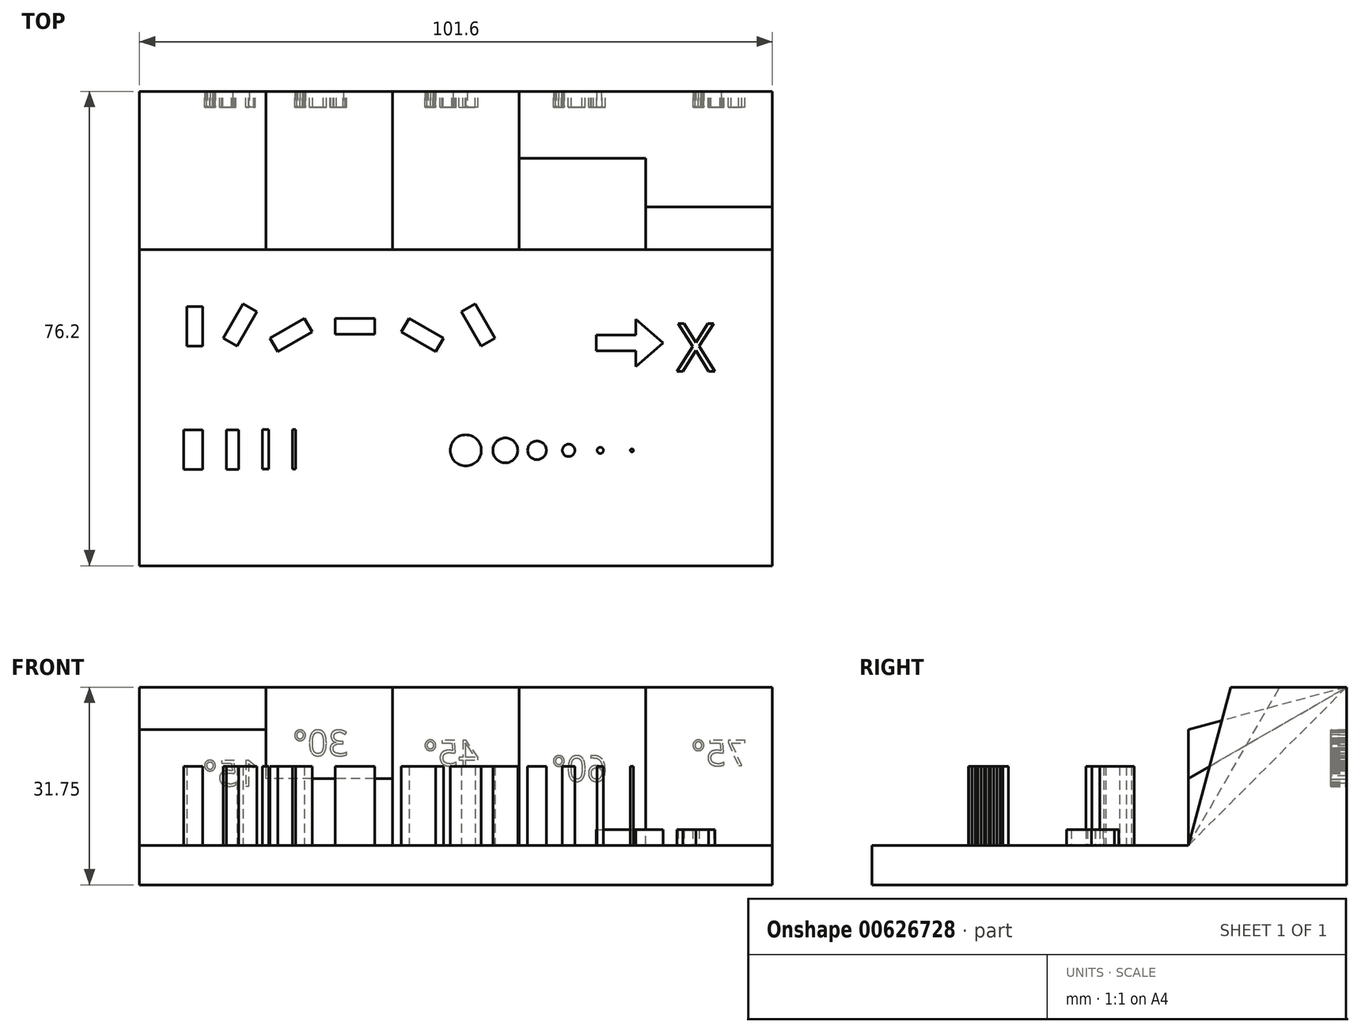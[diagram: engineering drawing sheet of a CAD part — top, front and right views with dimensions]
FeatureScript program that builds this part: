
annotation { "Feature Type Name" : "Feature", "Feature Type Description" : "" }
export const myFeature = defineFeature(function(context is Context, id is Id, definition is map)
    precondition{}
    {
        {
            var Q0;
            Q0=qCreatedBy(makeId("Top.planeOp"),FACE);
            var sketch = newSketch(context, id + "F0", { "sketchPlane" : qUnion([Q0])});
            skLineSegment(sketch, "E0.bottom", {"start": v(-49.6, 47.88) * mm, "end": v(52, 47.88) * mm});
            skLineSegment(sketch, "E0.top", {"start": v(-49.6, -28.32) * mm, "end": v(52, -28.32) * mm});
            skLineSegment(sketch, "E0.left", {"start": v(-49.6, 47.88) * mm, "end": v(-49.6, -28.32) * mm});
            skLineSegment(sketch, "E0.right", {"start": v(52, 47.88) * mm, "end": v(52, -28.32) * mm});
            skSolve(sketch);
        }
        {
            var Q0;
            Q0=makeQuery(id+"F0.imprint","IMPRINT",FACE,{"disambiguationData":[TD([[makeQuery(id+"F0.imprint","IMPRINT",EDGE,{"derivedFrom":sQuery(id+"F0.wireOp",EDGE,"E0.bottom")}),-1.0]])]});
            extrude(context, id + "F1", {"entities" : qUnion([Q0]), "depth" : 6.35 * mm, "offsetDistance" : 25.4 * mm});
        }
        {
            var Q0;
            Q0=makeQuery(id+"F1.opExtrude","CAP_FACE",FACE,{"disambiguationData":[OSD([sQuery(id+"F0.wireOp",EDGE,"E0.bottom"),sQuery(id+"F0.wireOp",EDGE,"E0.top"),sQuery(id+"F0.wireOp",EDGE,"E0.left"),sQuery(id+"F0.wireOp",EDGE,"E0.right")])],"isStart":false});
            var sketch = newSketch(context, id + "F2", { "sketchPlane" : qUnion([Q0])});
            skLineSegment(sketch, "E1.bottom", {"start": v(-49.6, 47.88) * mm, "end": v(52, 47.88) * mm});
            skLineSegment(sketch, "E1.top", {"start": v(-49.6, 22.48) * mm, "end": v(52, 22.48) * mm});
            skLineSegment(sketch, "E1.left", {"start": v(-49.6, 47.88) * mm, "end": v(-49.6, 22.48) * mm});
            skLineSegment(sketch, "E1.right", {"start": v(52, 47.88) * mm, "end": v(52, 22.48) * mm});
            skSolve(sketch);
        }
        {
            var Q0;
            Q0 = qSketchRegion(id + "F2", true);
            extrude(context, id + "F3", {"entities" : qUnion([Q0]), "operationType" : NewBodyOperationType.ADD, "depth" : 25.4 * mm, "offsetDistance" : 25.4 * mm});
        }
        {
            var Q0;
            Q0=makeQuery(id+"F3.boolean.opBoolean","MERGE",FACE,{"derivedFrom":[makeQuery(id+"F1.opExtrude","SWEPT_FACE",FACE,{"disambiguationData":[OSD([sQuery(id+"F0.wireOp",EDGE,"E0.left")])]}),makeQuery(id+"F3.opExtrude","SWEPT_FACE",FACE,{"disambiguationData":[OSD([sQuery(id+"F2.wireOp",EDGE,"E1.left")])]})]});
            var sketch = newSketch(context, id + "F4", { "sketchPlane" : qUnion([Q0])});
            skLineSegment(sketch, "E2", {"start": v(-47.88, 31.75) * mm, "end": v(-22.48, 24.94) * mm});
            skLineSegment(sketch, "E3", {"start": v(-22.48, 24.94) * mm, "end": v(-22.48, 31.75) * mm});
            skLineSegment(sketch, "E4", {"start": v(-22.48, 31.75) * mm, "end": v(-47.88, 31.75) * mm});
            skSolve(sketch);
        }
        {
            var Q0;
            Q0 = qSketchRegion(id + "F4", true);
            extrude(context, id + "F5", {"entities" : qUnion([Q0]), "operationType" : NewBodyOperationType.REMOVE, "oppositeDirection" : true, "depth" : 20.32 * mm, "offsetDistance" : 25.4 * mm});
        }
        {
            var Q0;
            Q0=makeQuery(id+"F5.boolean.opBoolean","COPY",FACE,{"derivedFrom":makeQuery(id+"F5.opExtrude","CAP_FACE",FACE,{"disambiguationData":[OSD([sQuery(id+"F4.wireOp",EDGE,"E2"),sQuery(id+"F4.wireOp",EDGE,"E3"),sQuery(id+"F4.wireOp",EDGE,"E4")])],"isStart":false})});
            var sketch = newSketch(context, id + "F6", { "sketchPlane" : qUnion([Q0])});
            skLineSegment(sketch, "E5", {"start": v(-47.88, 31.75) * mm, "end": v(-22.48, 31.75) * mm});
            skLineSegment(sketch, "E6", {"start": v(-22.48, 31.75) * mm, "end": v(-22.48, 17.09) * mm});
            skLineSegment(sketch, "E7", {"start": v(-22.48, 17.09) * mm, "end": v(-47.88, 31.75) * mm});
            skSolve(sketch);
        }
        {
            var Q0;
            Q0 = qSketchRegion(id + "F6", true);
            extrude(context, id + "F7", {"entities" : qUnion([Q0]), "operationType" : NewBodyOperationType.REMOVE, "oppositeDirection" : true, "depth" : 20.32 * mm, "offsetDistance" : 25.4 * mm});
        }
        {
            var Q0;
            Q0=makeQuery(id+"F7.boolean.opBoolean","COPY",FACE,{"derivedFrom":makeQuery(id+"F7.opExtrude","CAP_FACE",FACE,{"disambiguationData":[OSD([sQuery(id+"F6.wireOp",EDGE,"E5"),sQuery(id+"F6.wireOp",EDGE,"E6"),sQuery(id+"F6.wireOp",EDGE,"E7")])],"isStart":false})});
            var sketch = newSketch(context, id + "F8", { "sketchPlane" : qUnion([Q0])});
            skLineSegment(sketch, "E8", {"start": v(-47.88, 31.75) * mm, "end": v(-22.48, 31.75) * mm});
            skLineSegment(sketch, "E9", {"start": v(-22.48, 31.75) * mm, "end": v(-22.48, 6.35) * mm});
            skLineSegment(sketch, "E10", {"start": v(-22.48, 6.35) * mm, "end": v(-47.88, 31.75) * mm});
            skSolve(sketch);
        }
        {
            var Q0;
            Q0 = qSketchRegion(id + "F8", true);
            extrude(context, id + "F9", {"entities" : qUnion([Q0]), "operationType" : NewBodyOperationType.REMOVE, "oppositeDirection" : true, "depth" : 20.32 * mm, "offsetDistance" : 25.4 * mm});
        }
        {
            var Q0;
            Q0=makeQuery(id+"F9.boolean.opBoolean","COPY",FACE,{"derivedFrom":makeQuery(id+"F9.opExtrude","CAP_FACE",FACE,{"disambiguationData":[OSD([sQuery(id+"F8.wireOp",EDGE,"E8"),sQuery(id+"F8.wireOp",EDGE,"E9"),sQuery(id+"F8.wireOp",EDGE,"E10")])],"isStart":false})});
            var sketch = newSketch(context, id + "F10", { "sketchPlane" : qUnion([Q0])});
            skLineSegment(sketch, "E11", {"start": v(-22.48, 31.75) * mm, "end": v(-22.48, 6.35) * mm});
            skLineSegment(sketch, "E12", {"start": v(-22.48, 6.35) * mm, "end": v(-37.14, 31.75) * mm});
            skLineSegment(sketch, "E13", {"start": v(-37.14, 31.75) * mm, "end": v(-22.48, 31.75) * mm});
            skSolve(sketch);
        }
        {
            var Q0;
            Q0 = qSketchRegion(id + "F10", true);
            extrude(context, id + "F11", {"entities" : qUnion([Q0]), "operationType" : NewBodyOperationType.REMOVE, "oppositeDirection" : true, "depth" : 20.32 * mm, "offsetDistance" : 25.4 * mm});
        }
        {
            var Q0;
            Q0=makeQuery(id+"F11.boolean.opBoolean","COPY",FACE,{"derivedFrom":makeQuery(id+"F11.opExtrude","CAP_FACE",FACE,{"disambiguationData":[OSD([sQuery(id+"F10.wireOp",EDGE,"E11"),sQuery(id+"F10.wireOp",EDGE,"E12"),sQuery(id+"F10.wireOp",EDGE,"E13")])],"isStart":false})});
            var sketch = newSketch(context, id + "F12", { "sketchPlane" : qUnion([Q0])});
            skLineSegment(sketch, "E14", {"start": v(-22.48, 31.75) * mm, "end": v(-22.48, 6.35) * mm});
            skLineSegment(sketch, "E15", {"start": v(-22.48, 6.35) * mm, "end": v(-29.28, 31.75) * mm});
            skLineSegment(sketch, "E16", {"start": v(-29.28, 31.75) * mm, "end": v(-22.48, 31.75) * mm});
            skSolve(sketch);
        }
        {
            var Q0;
            Q0 = qSketchRegion(id + "F12", true);
            extrude(context, id + "F13", {"entities" : qUnion([Q0]), "operationType" : NewBodyOperationType.REMOVE, "oppositeDirection" : true, "depth" : 25.4 * mm, "offsetDistance" : 25.4 * mm});
        }
        {
            var Q0;
            Q0=makeQuery(id+"F3.boolean.opBoolean","MERGE",FACE,{"derivedFrom":[makeQuery(id+"F1.opExtrude","SWEPT_FACE",FACE,{"disambiguationData":[OSD([sQuery(id+"F0.wireOp",EDGE,"E0.bottom")])]}),makeQuery(id+"F3.opExtrude","SWEPT_FACE",FACE,{"disambiguationData":[OSD([sQuery(id+"F2.wireOp",EDGE,"E1.bottom")])]})]});
            var sketch = newSketch(context, id + "F14", { "sketchPlane" : qUnion([Q0])});
            skText(sketch, "E17", { "text": "75°", "fontName": "OpenSans-Regular.ttf"});
            skText(sketch, "E18", { "text": "60°", "fontName": "OpenSans-Regular.ttf"});
            skText(sketch, "E19", { "text": "45°", "fontName": "OpenSans-Regular.ttf"});
            skText(sketch, "E20", { "text": "30°", "fontName": "OpenSans-Regular.ttf"});
            skText(sketch, "E21", { "text": "15°", "fontName": "OpenSans-Regular.ttf"});
            skPoint(sketch, "E22", {"position": v(49.6, 15.87) * mm});
            const initialGuessF14  = {"E17": [-0.0479, 0.01913, 1, 0, 0.00412], "E18": [-0.0255, 0.01662, 1, 0, 0.00412], "E19": [-0.00488, 0.01913, 1, 0, 0.00412], "E20": [0.01604, 0.02074, 1, 0, 0.00412], "E21": [0.0305, 0.01587, 1, 0, 0.00412]};
            skSetInitialGuess(sketch, initialGuessF14);
            skSolve(sketch);
        }
        {
            var Q0;
            Q0=makeQuery(id+"F1.opExtrude","CAP_FACE",FACE,{"disambiguationData":[OSD([sQuery(id+"F0.wireOp",EDGE,"E0.bottom"),sQuery(id+"F0.wireOp",EDGE,"E0.top"),sQuery(id+"F0.wireOp",EDGE,"E0.left"),sQuery(id+"F0.wireOp",EDGE,"E0.right")])],"isStart":false});
            var sketch = newSketch(context, id + "F15", { "sketchPlane" : qUnion([Q0])});
            skLineSegment(sketch, "E23.bottom", {"start": v(-32.96, 13.74) * mm, "end": v(-30.76, 12.47) * mm});
            skLineSegment(sketch, "E23.top", {"start": v(-36.13, 8.24) * mm, "end": v(-33.93, 6.97) * mm});
            skLineSegment(sketch, "E23.left", {"start": v(-32.96, 13.74) * mm, "end": v(-36.13, 8.24) * mm});
            skLineSegment(sketch, "E23.right", {"start": v(-30.76, 12.47) * mm, "end": v(-33.93, 6.97) * mm});
            skLineSegment(sketch, "E24.bottom", {"start": v(-42, 13.32) * mm, "end": v(-39.46, 13.32) * mm});
            skLineSegment(sketch, "E24.top", {"start": v(-42, 6.97) * mm, "end": v(-39.46, 6.97) * mm});
            skLineSegment(sketch, "E24.left", {"start": v(-42, 13.32) * mm, "end": v(-42, 6.97) * mm});
            skLineSegment(sketch, "E24.right", {"start": v(-39.46, 13.32) * mm, "end": v(-39.46, 6.97) * mm});
            skLineSegment(sketch, "E25.bottom", {"start": v(-23.15, 11.42) * mm, "end": v(-21.88, 9.22) * mm});
            skLineSegment(sketch, "E25.top", {"start": v(-28.65, 8.24) * mm, "end": v(-27.38, 6.04) * mm});
            skLineSegment(sketch, "E25.left", {"start": v(-23.15, 11.42) * mm, "end": v(-28.65, 8.24) * mm});
            skLineSegment(sketch, "E25.right", {"start": v(-21.88, 9.22) * mm, "end": v(-27.38, 6.04) * mm});
            skLineSegment(sketch, "E26.bottom", {"start": v(-11.85, 11.42) * mm, "end": v(-11.85, 8.88) * mm});
            skLineSegment(sketch, "E26.top", {"start": v(-18.2, 11.42) * mm, "end": v(-18.2, 8.88) * mm});
            skLineSegment(sketch, "E26.left", {"start": v(-11.85, 11.42) * mm, "end": v(-18.2, 11.42) * mm});
            skLineSegment(sketch, "E26.right", {"start": v(-11.85, 8.88) * mm, "end": v(-18.2, 8.88) * mm});
            skLineSegment(sketch, "E27.bottom", {"start": v(-0.77, 8.24) * mm, "end": v(-2.04, 6.04) * mm});
            skLineSegment(sketch, "E27.top", {"start": v(-6.27, 11.42) * mm, "end": v(-7.54, 9.22) * mm});
            skLineSegment(sketch, "E27.left", {"start": v(-0.77, 8.24) * mm, "end": v(-6.27, 11.42) * mm});
            skLineSegment(sketch, "E27.right", {"start": v(-2.04, 6.04) * mm, "end": v(-7.54, 9.22) * mm});
            skLineSegment(sketch, "E28.bottom", {"start": v(7.45, 8.24) * mm, "end": v(5.25, 6.97) * mm});
            skLineSegment(sketch, "E28.top", {"start": v(4.28, 13.74) * mm, "end": v(2.08, 12.47) * mm});
            skLineSegment(sketch, "E28.left", {"start": v(7.45, 8.24) * mm, "end": v(4.28, 13.74) * mm});
            skLineSegment(sketch, "E28.right", {"start": v(5.25, 6.97) * mm, "end": v(2.08, 12.47) * mm});
            skSolve(sketch);
        }
        {
            var Q0;
            Q0 = qSketchRegion(id + "F15", true);
            extrude(context, id + "F16", {"entities" : qUnion([Q0]), "operationType" : NewBodyOperationType.ADD, "depth" : 12.7 * mm, "offsetDistance" : 25.4 * mm});
        }
        {
            var Q0;
            Q0=makeQuery(id+"F1.opExtrude","CAP_FACE",FACE,{"disambiguationData":[OSD([sQuery(id+"F0.wireOp",EDGE,"E0.bottom"),sQuery(id+"F0.wireOp",EDGE,"E0.top"),sQuery(id+"F0.wireOp",EDGE,"E0.left"),sQuery(id+"F0.wireOp",EDGE,"E0.right")])],"isStart":false});
            var sketch = newSketch(context, id + "F17", { "sketchPlane" : qUnion([Q0])});
            skLineSegment(sketch, "E29.bottom", {"start": v(-42.46, -6.48) * mm, "end": v(-39.46, -6.48) * mm});
            skLineSegment(sketch, "E29.top", {"start": v(-42.46, -12.83) * mm, "end": v(-39.46, -12.83) * mm});
            skLineSegment(sketch, "E29.left", {"start": v(-42.46, -6.48) * mm, "end": v(-42.46, -12.83) * mm});
            skLineSegment(sketch, "E29.right", {"start": v(-39.46, -6.48) * mm, "end": v(-39.46, -12.83) * mm});
            skLineSegment(sketch, "E30.bottom", {"start": v(-35.65, -6.5) * mm, "end": v(-33.65, -6.5) * mm});
            skLineSegment(sketch, "E30.top", {"start": v(-35.65, -12.84) * mm, "end": v(-33.65, -12.84) * mm});
            skLineSegment(sketch, "E30.left", {"start": v(-35.65, -6.5) * mm, "end": v(-35.65, -12.84) * mm});
            skLineSegment(sketch, "E30.right", {"start": v(-33.65, -6.5) * mm, "end": v(-33.65, -12.84) * mm});
            skLineSegment(sketch, "E31.bottom", {"start": v(-29.84, -6.43) * mm, "end": v(-28.84, -6.43) * mm});
            skLineSegment(sketch, "E31.top", {"start": v(-29.84, -12.78) * mm, "end": v(-28.84, -12.78) * mm});
            skLineSegment(sketch, "E31.left", {"start": v(-29.84, -6.43) * mm, "end": v(-29.84, -12.78) * mm});
            skLineSegment(sketch, "E31.right", {"start": v(-28.84, -6.43) * mm, "end": v(-28.84, -12.78) * mm});
            skSolve(sketch);
        }
        {
            var Q0;
            Q0 = qSketchRegion(id + "F17", true);
            extrude(context, id + "F18", {"entities" : qUnion([Q0]), "operationType" : NewBodyOperationType.ADD, "depth" : 12.7 * mm, "offsetDistance" : 25.4 * mm});
        }
        {
            var Q0;
            Q0=makeQuery(id+"F1.opExtrude","CAP_FACE",FACE,{"disambiguationData":[OSD([sQuery(id+"F0.wireOp",EDGE,"E0.bottom"),sQuery(id+"F0.wireOp",EDGE,"E0.top"),sQuery(id+"F0.wireOp",EDGE,"E0.left"),sQuery(id+"F0.wireOp",EDGE,"E0.right")])],"isStart":false});
            var sketch = newSketch(context, id + "F19", { "sketchPlane" : qUnion([Q0])});
            skCircle(sketch, "E32", {"center": v(14.22, -9.79) * mm, "radius": 1.5 * mm});
            skCircle(sketch, "E33", {"center": v(19.3, -9.79) * mm, "radius": 1 * mm});
            skCircle(sketch, "E34", {"center": v(29.46, -9.79) * mm, "radius": 0.25 * mm});
            skCircle(sketch, "E35", {"center": v(24.38, -9.79) * mm, "radius": 0.5 * mm});
            skLineSegment(sketch, "E36.bottom", {"start": v(-25.03, -6.43) * mm, "end": v(-24.53, -6.43) * mm});
            skLineSegment(sketch, "E36.top", {"start": v(-25.03, -12.78) * mm, "end": v(-24.53, -12.78) * mm});
            skLineSegment(sketch, "E36.left", {"start": v(-25.03, -6.43) * mm, "end": v(-25.03, -12.78) * mm});
            skLineSegment(sketch, "E36.right", {"start": v(-24.53, -6.43) * mm, "end": v(-24.53, -12.78) * mm});
            skCircle(sketch, "E37", {"center": v(9.14, -9.79) * mm, "radius": 2 * mm});
            skCircle(sketch, "E38", {"center": v(2.8, -9.79) * mm, "radius": 2.5 * mm});
            skSolve(sketch);
        }
        {
            var Q0;
            Q0 = qSketchRegion(id + "F19", true);
            extrude(context, id + "F20", {"entities" : qUnion([Q0]), "operationType" : NewBodyOperationType.ADD, "depth" : 12.7 * mm, "offsetDistance" : 25.4 * mm});
        }
        {
            var Q0;
            Q0=makeQuery(id+"F1.opExtrude","CAP_FACE",FACE,{"disambiguationData":[OSD([sQuery(id+"F0.wireOp",EDGE,"E0.bottom"),sQuery(id+"F0.wireOp",EDGE,"E0.top"),sQuery(id+"F0.wireOp",EDGE,"E0.left"),sQuery(id+"F0.wireOp",EDGE,"E0.right")])],"isStart":false});
            var sketch = newSketch(context, id + "F21", { "sketchPlane" : qUnion([Q0])});
            skLineSegment(sketch, "E39.bottom", {"start": v(23.72, 8.74) * mm, "end": v(30.07, 8.74) * mm});
            skLineSegment(sketch, "E39.top", {"start": v(23.72, 6.2) * mm, "end": v(30.07, 6.2) * mm});
            skLineSegment(sketch, "E39.left", {"start": v(23.72, 8.74) * mm, "end": v(23.72, 6.2) * mm});
            skLineSegment(sketch, "E39.right", {"start": v(30.07, 8.74) * mm, "end": v(30.07, 6.2) * mm});
            skLineSegment(sketch, "E40", {"start": v(30.07, 8.74) * mm, "end": v(30.07, 11.28) * mm});
            skLineSegment(sketch, "E41", {"start": v(30.07, 11.28) * mm, "end": v(34.46, 7.47) * mm});
            skPoint(sketch, "E41.endSnap0", {"position": v(30.07, 7.47) * mm});
            skLineSegment(sketch, "E42", {"start": v(34.46, 7.47) * mm, "end": v(30.07, 3.66) * mm});
            skLineSegment(sketch, "E43", {"start": v(30.07, 3.66) * mm, "end": v(30.07, 6.2) * mm});
            skText(sketch, "E44", { "text": "X\n", "fontName": "OpenSans-Regular.ttf"});
            const initialGuessF21  = {"E44": [0.03664, 0.0029, 1, 0, 0.00773]};
            skSetInitialGuess(sketch, initialGuessF21);
            skSolve(sketch);
        }
        {
            var Q0;
            Q0 = qSketchRegion(id + "F21", true);
            extrude(context, id + "F22", {"entities" : qUnion([Q0]), "operationType" : NewBodyOperationType.ADD, "depth" : 2.54 * mm, "offsetDistance" : 25.4 * mm});
        }
        {
            var Q0;
            Q0 = qSketchRegion(id + "F14", true);
            extrude(context, id + "F23", {"entities" : qUnion([Q0]), "operationType" : NewBodyOperationType.REMOVE, "oppositeDirection" : true, "depth" : 2.54 * mm, "offsetDistance" : 25.4 * mm});
        }
    });
